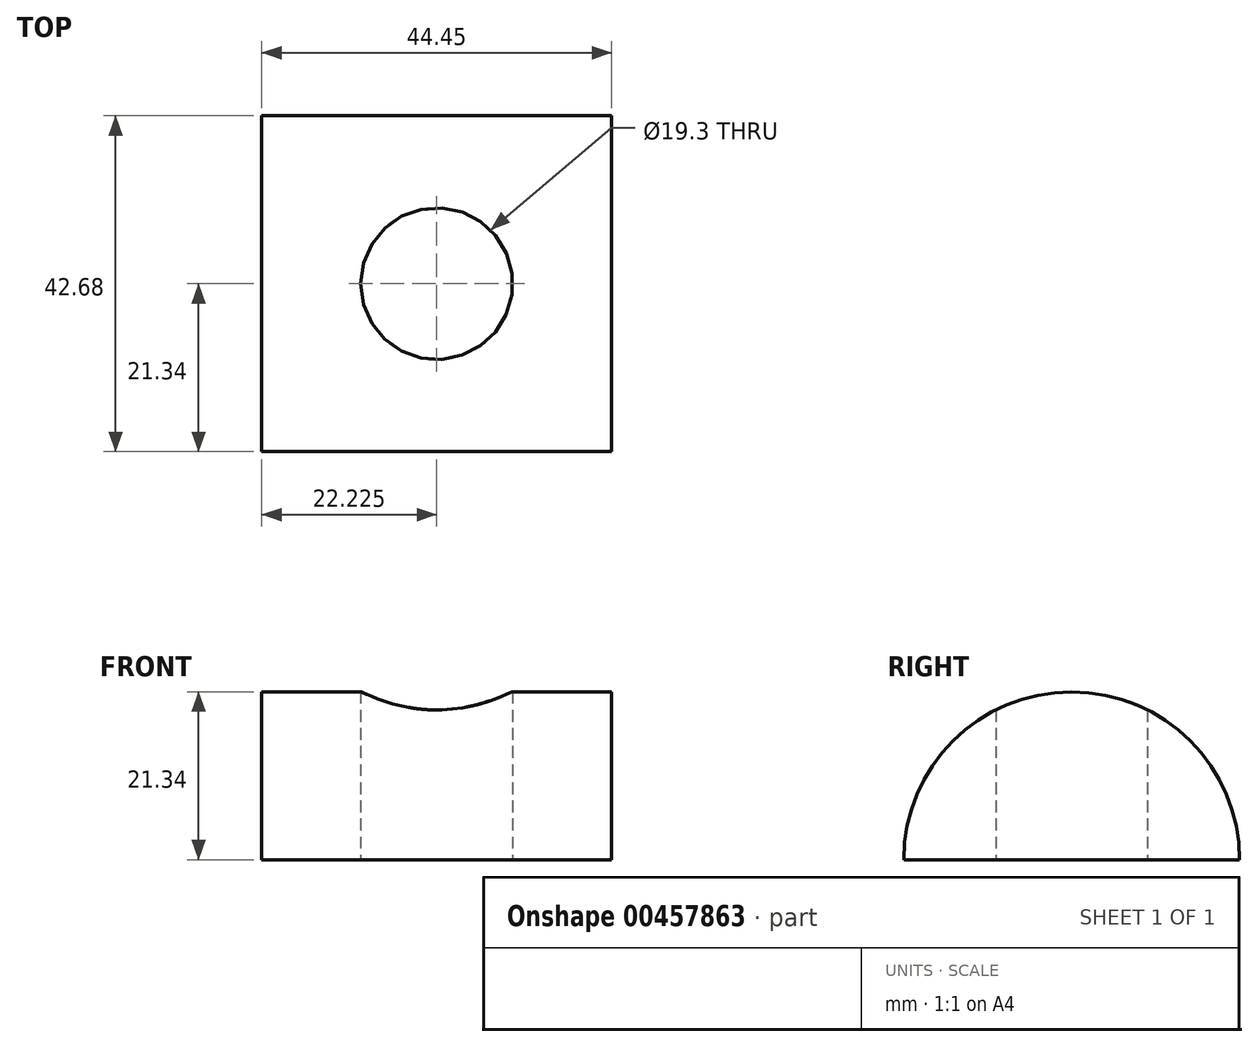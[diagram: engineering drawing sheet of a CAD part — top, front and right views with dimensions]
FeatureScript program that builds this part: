
annotation { "Feature Type Name" : "Feature", "Feature Type Description" : "" }
export const myFeature = defineFeature(function(context is Context, id is Id, definition is map)
    precondition{}
    {
        {
            var Q0;
            Q0=qCreatedBy(makeId("Right.planeOp"),FACE);
            var sketch = newSketch(context, id + "F0", { "sketchPlane" : qUnion([Q0])});
            skArc(sketch, "E0", {"start": v(21.34, 0) * mm, "mid": v(0, 21.34) * mm, "end": v(-21.34, 0) * mm});
            skLineSegment(sketch, "E1", {"start": v(-21.34, 0) * mm, "end": v(21.34, 0) * mm});
            skSolve(sketch);
        }
        {
            var Q0;
            Q0=makeQuery(id+"F0.imprint","IMPRINT",FACE,{"disambiguationData":[TD([[makeQuery(id+"F0.imprint","IMPRINT",EDGE,{"derivedFrom":sQuery(id+"F0.wireOp",EDGE,"E0")}),1.0]])]});
            extrude(context, id + "F1", {"entities" : qUnion([Q0]), "oppositeDirection" : true, "depth" : 44.45 * mm});
        }
        {
            var Q0;
            Q0=makeQuery(id+"F1.opExtrude","SWEPT_FACE",FACE,{"disambiguationData":[OSD([sQuery(id+"F0.wireOp",EDGE,"E1")])]});
            var sketch = newSketch(context, id + "F2", { "sketchPlane" : qUnion([Q0])});
            skCircle(sketch, "E2", {"center": v(-22.23, 0) * mm, "radius": 9.65 * mm});
            skSolve(sketch);
        }
        {
            var Q0;
            Q0=makeQuery(id+"F2.imprint","IMPRINT",FACE,{"disambiguationData":[TD([[makeQuery(id+"F2.imprint","IMPRINT",EDGE,{"derivedFrom":sQuery(id+"F2.wireOp",EDGE,"E2")}),1.0]])]});
            extrude(context, id + "F3", {"entities" : qUnion([Q0]), "operationType" : NewBodyOperationType.REMOVE, "endBound" : BoundingType.THROUGH_ALL, "oppositeDirection" : true, "depth" : 25.4 * mm});
        }
    });
